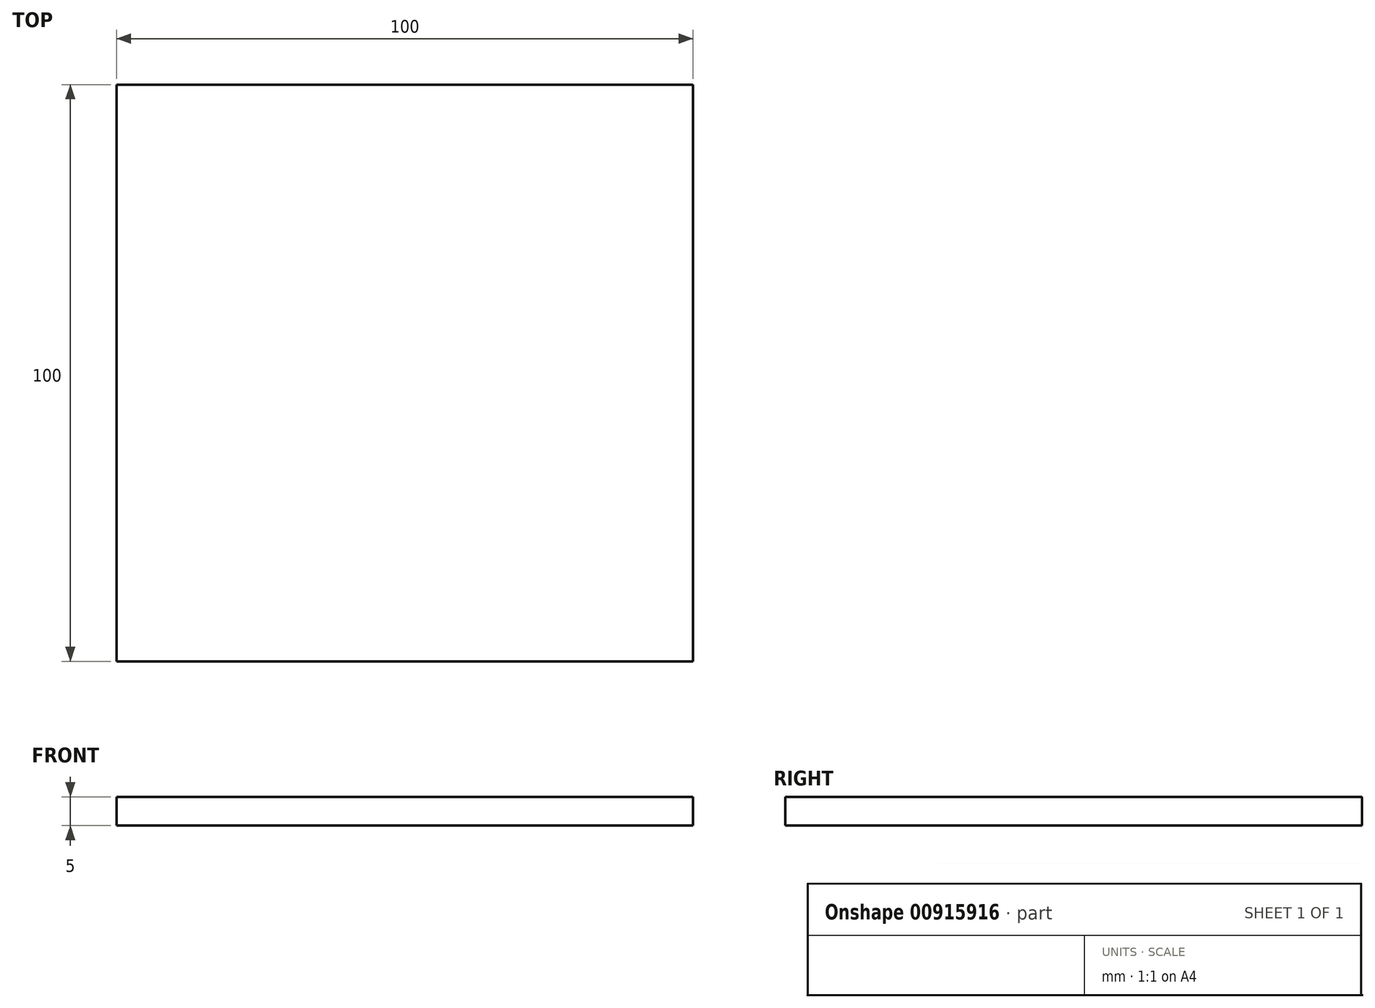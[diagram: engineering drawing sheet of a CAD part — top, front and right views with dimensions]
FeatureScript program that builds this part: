
annotation { "Feature Type Name" : "Feature", "Feature Type Description" : "" }
export const myFeature = defineFeature(function(context is Context, id is Id, definition is map)
    precondition{}
    {
        {
            var Q0;
            Q0=qCreatedBy(makeId("Top.planeOp"),FACE);
            var sketch = newSketch(context, id + "F0", { "sketchPlane" : qUnion([Q0])});
            skLineSegment(sketch, "E0.bottom", {"start": v(-50, 50) * mm, "end": v(50, 50) * mm});
            skLineSegment(sketch, "E0.top", {"start": v(-50, -50) * mm, "end": v(50, -50) * mm});
            skLineSegment(sketch, "E0.left", {"start": v(-50, 50) * mm, "end": v(-50, -50) * mm});
            skLineSegment(sketch, "E0.right", {"start": v(50, 50) * mm, "end": v(50, -50) * mm});
            skPoint(sketch, "E0.middle", {"position": v(0, 0) * mm});
            skSolve(sketch);
        }
        {
            var Q0;
            Q0=makeQuery(id+"F0.imprint","IMPRINT",FACE,{"disambiguationData":[TD([[makeQuery(id+"F0.imprint","IMPRINT",EDGE,{"derivedFrom":sQuery(id+"F0.wireOp",EDGE,"E0.bottom")}),-1.0]])]});
            extrude(context, id + "F1", {"entities" : qUnion([Q0]), "depth" : 5 * mm, "offsetDistance" : 25 * mm});
        }
    });
